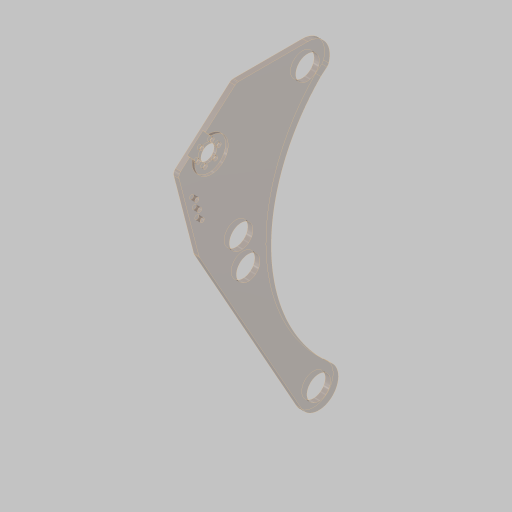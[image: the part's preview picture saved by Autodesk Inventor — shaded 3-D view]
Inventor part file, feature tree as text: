
AUTODESK INVENTOR PART (.ipt)
format: ipt  version: 2023.5 (Build 275446000, 446)  size: 258,560 bytes
history: native  units: in
note: dims shown in document units (in); Inventor stores cm internally (conversion verified against a paired STEP export)
features: sketch x7, extrude x4, projected_geometry x4, hole x2, fillet x1
ambient origin geometry x8: Origin, YZ Plane, XZ Plane, XY Plane, X Axis, Y Axis, Z Axis, Center Point
bodies: Body1 (feature_tree)
feature tree (18):
  sketch  "Sketch1"  dims[d0=16.0in d1=3.0in]
  extrude  "Extrusion2"  Depth=3.0in
  hole  "Hole2"  [1 undecoded]
  extrude  "Extrusion3"  Depth=7.0in
  fillet  "Fillet1"  Radius=1.125in
  extrude  "Extrusion4"  Depth=0.375in
  extrude  "Extrusion5"  Depth=3.75in
  hole  "Hole4"  [1 undecoded]
  sketch  "Sketch4"  dims[d2=0.25in d4=4.5in]
  sketch  "Sketch5"  dims[d5=11.875in d6=7.0in d27=1.125in]
  sketch  "Sketch6"  dims[d29=0.375in d31=4.0in]
  projected_geometry  "Projected Loop1"
  sketch  "Sketch8"  dims[d33=4.0in d35=3.75in]
  sketch  "Sketch9"  dims[d36=0.25in d37=0.0in d39=0.5in]
  sketch  "Sketch10"  dims[d41=0.201in d42=0.75in d43=0.385in d44=0.25in d45=0.5635in d46=1.0in d47=0.8108in d51=6.5in d52=11.0in d53=1.2075in d57=1.0in d58=11.75in d59=12.75in d60=1.25in d63=1.0in d64=0.0in d65=0.5in d66=0.26in d76=0.602in d77=1.5in d78=2.256in d79=4.7708in d81=1.0in d83=0.75in d84=1.125in d85=6.2598in d87=1.5in d88=7.4409in d90=1.0in d91=0.0in d93=1.6in d94=0.125in d95=0.0in d96=1.0in d97=1.0in d98=2.3622in d100=360.0deg d102=0.201in d103=0.198in d104=0.385in d105=0.25in d106=0.5635in d107=1.0in d108=0.8108in d110=0.75in d111=1.25in]
  projected_geometry  "Project Cut Edges1"
  projected_geometry  "Project Cut Edges2"
  projected_geometry  "Project Cut Edges3"
note: 2 required parameter values undecoded (feature->parameter linkage not recoverable at this tier; creation-order binding heuristic only, values carry confidence <= 0.55)
